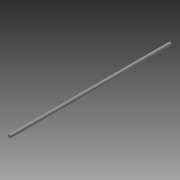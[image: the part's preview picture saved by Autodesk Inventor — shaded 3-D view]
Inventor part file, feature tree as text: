
AUTODESK INVENTOR PART (.ipt)
format: ipt  version: 2015 (Build 190159000, 159)  size: 64,512 bytes
history: native  units: in
note: dims shown in document units (in); Inventor stores cm internally (conversion verified against a paired STEP export)
features: extrude x1, sketch x1
ambient origin geometry x8: Origin, YZ Plane, XZ Plane, XY Plane, X Axis, Y Axis, Z Axis, Center Point
bodies: Solid1 (feature_tree)
feature tree (2):
  extrude  "Extrusion1"  Depth=9.8425in TaperAngle=0.0deg
  sketch  "Sketch1"  dims[d0=0.1969in d1=9.8425in d2=0.0in]
